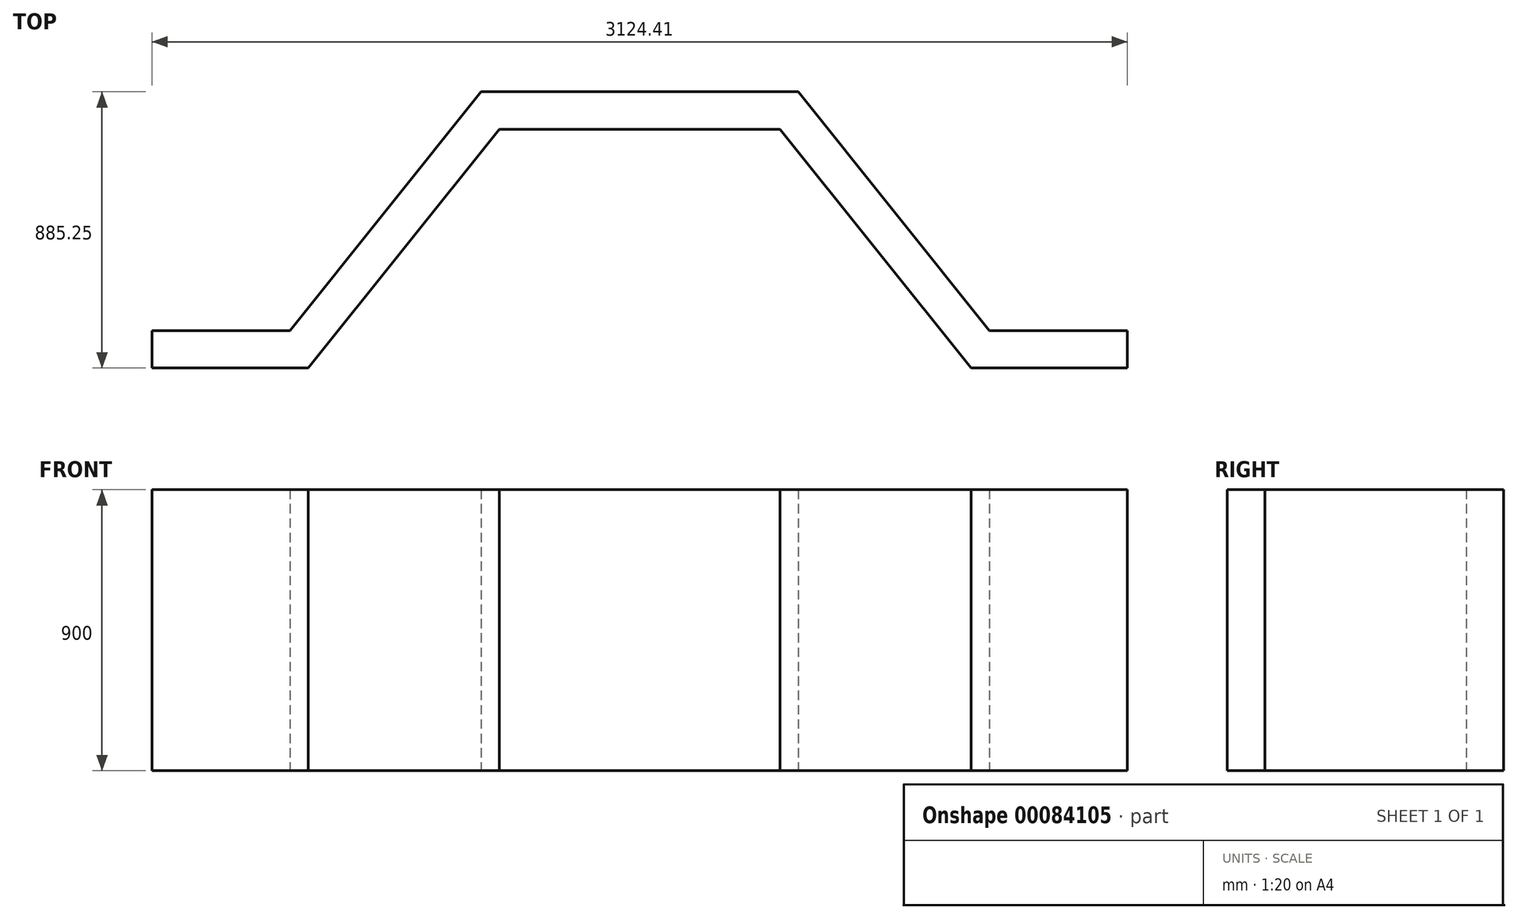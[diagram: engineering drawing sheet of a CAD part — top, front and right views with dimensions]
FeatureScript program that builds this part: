
annotation { "Feature Type Name" : "Feature", "Feature Type Description" : "" }
export const myFeature = defineFeature(function(context is Context, id is Id, definition is map)
    precondition{}
    {
        {
            var Q0;
            Q0=qCreatedBy(makeId("Top.planeOp"),FACE);
            var sketch = newSketch(context, id + "F0", { "sketchPlane" : qUnion([Q0])});
            skLineSegment(sketch, "E0", {"start": v(-255.75, -50.26) * mm, "end": v(244.25, -50.26) * mm});
            skLineSegment(sketch, "E1", {"start": v(244.25, -50.26) * mm, "end": v(856.46, 714.99) * mm});
            skLineSegment(sketch, "E2", {"start": v(856.46, 714.99) * mm, "end": v(1756.46, 714.99) * mm});
            skLineSegment(sketch, "E3", {"start": v(1756.46, 714.99) * mm, "end": v(2368.66, -50.26) * mm});
            skLineSegment(sketch, "E4", {"start": v(2368.66, -50.26) * mm, "end": v(2868.66, -50.26) * mm});
            skLineSegment(sketch, "E5", {"start": v(2868.66, -50.26) * mm, "end": v(2868.66, 69.74) * mm});
            skLineSegment(sketch, "E6", {"start": v(2868.66, 69.74) * mm, "end": v(2426.33, 69.74) * mm});
            skLineSegment(sketch, "E7", {"start": v(2426.33, 69.74) * mm, "end": v(1814.13, 834.99) * mm});
            skLineSegment(sketch, "E8", {"start": v(1814.13, 834.99) * mm, "end": v(798.78, 834.99) * mm});
            skLineSegment(sketch, "E9", {"start": v(798.78, 834.99) * mm, "end": v(186.58, 69.74) * mm});
            skLineSegment(sketch, "E10", {"start": v(186.58, 69.74) * mm, "end": v(-255.75, 69.74) * mm});
            skLineSegment(sketch, "E11", {"start": v(-255.75, 69.74) * mm, "end": v(-255.75, -50.26) * mm});
            skSolve(sketch);
        }
        {
            var Q0;
            Q0=makeQuery(id+"F0.imprint","IMPRINT",FACE,{"disambiguationData":[TD([[makeQuery(id+"F0.imprint","IMPRINT",EDGE,{"derivedFrom":sQuery(id+"F0.wireOp",EDGE,"E0")}),1.0]])]});
            extrude(context, id + "F1", {"entities" : qUnion([Q0]), "depth" : 900 * mm});
        }
    });
